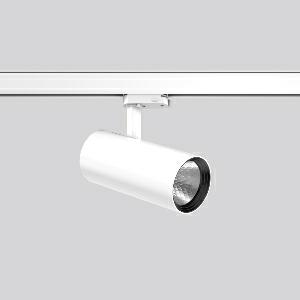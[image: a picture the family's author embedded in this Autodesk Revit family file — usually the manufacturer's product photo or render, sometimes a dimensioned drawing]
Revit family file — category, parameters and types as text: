
# Revit family: deecos_s_mini_742204_002_3_76_51ec
name_source: partatom
category: Lighting Fixtures
units: mm (PartAtom-declared; Revit-internal decimal feet)

## family parameters
Cut with Voids When Loaded = No
Host = Face
Light Source = No
Part Type = Normal
Room Calculation Point = No
Round Connector Dimension = Use Diameter
Shared = No

## types (1)
- DEECOS S mini (1 x LED Modul 935, 3600 lm, 3500)
    Apparent Load = 29 VA
    Approval mark = CE
    CIE Flux Codes = 99 100 100 100 100
    Color Rendering = 92
    Color Temperature = 3500
    Default Elevation = 1800 mm
    Description = Series: DEECOS S mini
LED surface-mounted projector in modern design with no visible cooling ribs. Housing: die-cast aluminium, powder-coated. Rotation range: 356°. Swivel range: 90°. Black plastic ring and recessed LED to prevent glare from the side. Optical assembly with reflector made of MIRO-Silver with 98% total light reflection for outstanding efficiency - can be changed without tools. Best colour rendering index Ra>90. With adapter for RZB 3-circuit DALI tracks. Suitable for Track on ceiling, Wall track. High quality converter without flickering and stroboscopic effect. The following accessories can be mounted without use of tools: interchangeable lenses, decorative glasses, honeycomb louvre, clear and frosted diffusers, white interchangeable plastic ring. 
Colour: traffic white, matt (RAL 9016)
Diameter: 87 mm
Height: 214 mm
Lamp: LED
Socket: without socket
Colour temperature: 3500K
Colour rendering index (CRI): 92
System power: 29 W
Rated luminous flux: 3600 lm
Luminous efficiency: 124 lm/W
Control gear: Converter, dimmable, DALI
Protection class: I
Type of protection: IP 20
    Height = 214 mm
    Lamp = 1 x LED Modul 935
    Lamp Light Flux = 3600 lm
    Lamp count = 1
    Length = 87 mm
    Lifetime = 50000 h
    Luminous efficacy = 124 lm/W
    Manufacturer = RZB
    ModVariant = No
    Model = 742204.002.3.76
    Mounting Place = Ceiling
    Mounting Type = Rail mounted
    Number of Poles = 1
    OnlyDefault = Yes
    Power Factor = 1
    Product Name = DEECOS S mini
    Product group = Track mounted projectors
    ProductGroupID = 301
    Protection Class = Protection class I
    Protection Degree = IP 20
    RLX_Detail_Level = 1
    RLX_Emergency_Light_Flux = 0 lm
    RLX_Emergency_Type = 0
    RLX_Emergency_Type_DB = No
    RlxData = <blob elided: 35425 chars, md5=e0e9d6e2>
    Socket = socket
    Standby Power = 0 W
    System Light Flux = 3600 lm
    System Power = 29 W
    Type Comments = Product without accessories
    Type Image = 741926.002.jpg
    URL = http://relux.com
    VarID = ---
    Voltage = 230 V
    Voltage Range = 220-240 V
    Weight = 0.00 kg
    Width = 0 mm  [stored 0 ft]

note: [stored X ft] marks values corroborated as IEEE doubles in the binary element streams (Revit-internal decimal feet)

## geometry (parser evidence)
native form markers: Blend x4, Sweep x13
no freeform markers — native parametric forms only
